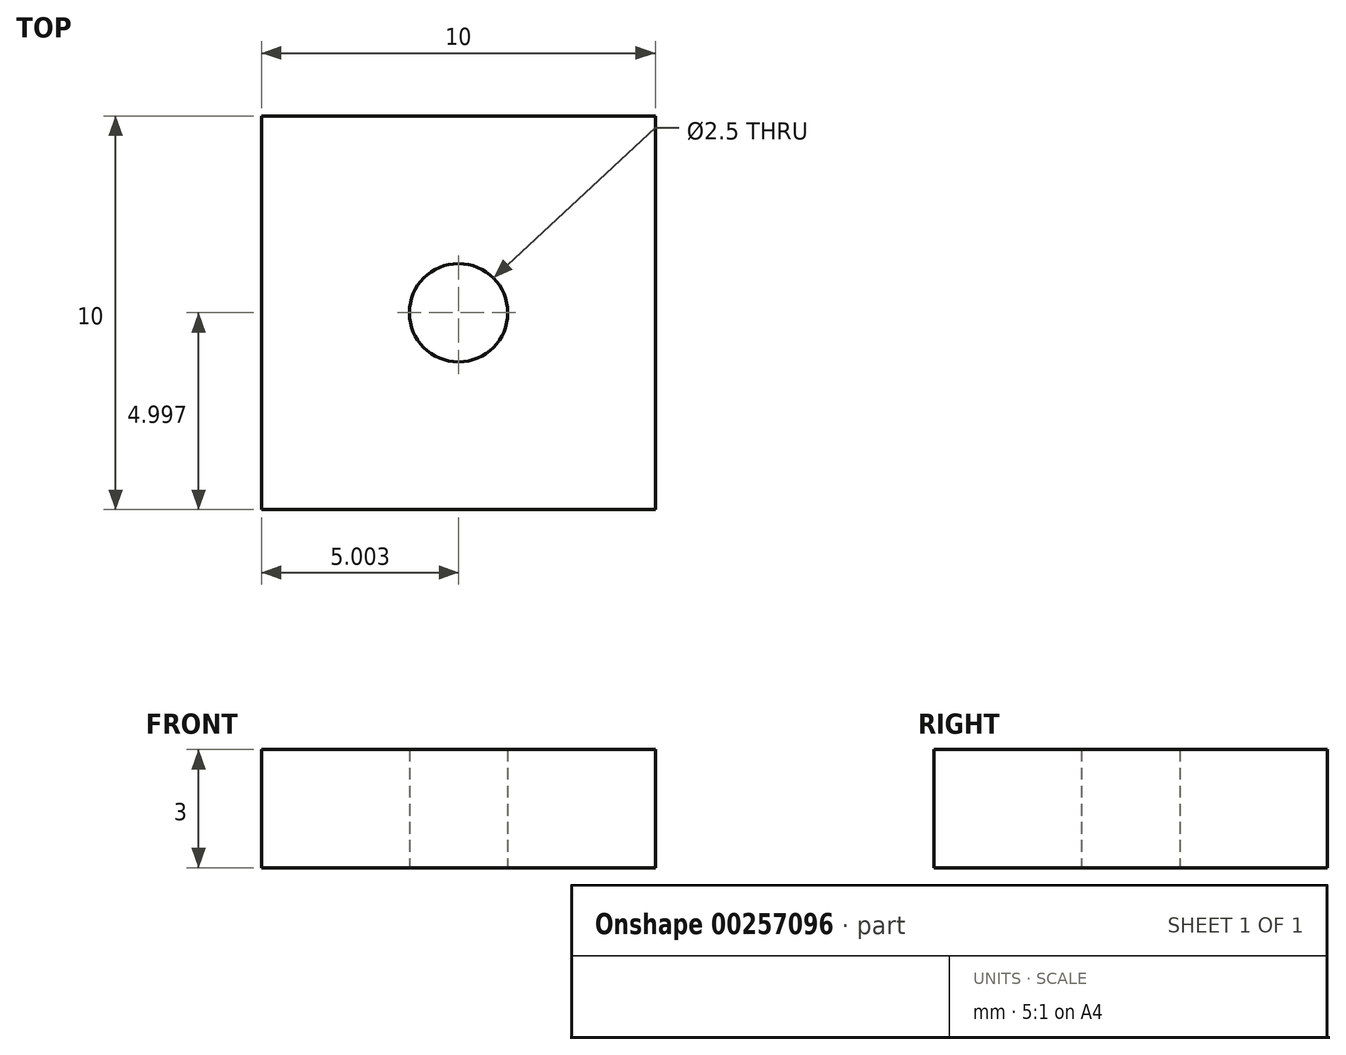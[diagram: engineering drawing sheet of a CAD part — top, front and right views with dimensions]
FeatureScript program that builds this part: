
annotation { "Feature Type Name" : "Feature", "Feature Type Description" : "" }
export const myFeature = defineFeature(function(context is Context, id is Id, definition is map)
    precondition{}
    {
        {
            var Q0;
            Q0=qCreatedBy(makeId("Top.planeOp"),FACE);
            var sketch = newSketch(context, id + "F0", { "sketchPlane" : qUnion([Q0])});
            skLineSegment(sketch, "E0.bottom", {"start": v(-4.78, 4.34) * mm, "end": v(5.22, 4.34) * mm});
            skLineSegment(sketch, "E0.top", {"start": v(-4.78, -5.66) * mm, "end": v(5.22, -5.66) * mm});
            skLineSegment(sketch, "E0.left", {"start": v(-4.78, 4.34) * mm, "end": v(-4.78, -5.66) * mm});
            skLineSegment(sketch, "E0.right", {"start": v(5.22, 4.34) * mm, "end": v(5.22, -5.66) * mm});
            skCircle(sketch, "E1", {"center": v(0.22, -0.66) * mm, "radius": 1.25 * mm});
            skSolve(sketch);
        }
        {
            var Q0;
            Q0=makeQuery(id+"F0.imprint","IMPRINT",FACE,{"disambiguationData":[TD([[makeQuery(id+"F0.imprint","IMPRINT",EDGE,{"derivedFrom":sQuery(id+"F0.wireOp",EDGE,"E0.bottom")}),-1.0]])]});
            extrude(context, id + "F1", {"entities" : qUnion([Q0]), "depth" : 3 * mm});
        }
    });
